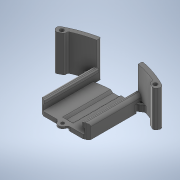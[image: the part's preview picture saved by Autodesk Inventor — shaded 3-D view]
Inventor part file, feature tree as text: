
AUTODESK INVENTOR PART (.ipt)
format: ipt  version: 2020 (Build 240168000, 168)  size: 1,011,712 bytes
history: native  units: mm
features: projected_geometry x25, other x11, sketch x11, extrude x10, fillet x3, chamfer x1
ambient origin geometry x8: Origin, YZ Plane, XZ Plane, XY Plane, X Axis, Y Axis, Z Axis, Center Point
bodies: Body1 (feature_tree)
feature tree (61):
  other  "Твердое тело1"
  sketch  "Эскиз1"
  other  "РабПлоскость4"
  sketch  "Эскиз2"
  other  "РабПлоскость5"
  sketch  "Эскиз3"
  other  "РабПлоскость6"
  sketch  "Эскиз4"
  other  "РабПлоскость7"
  sketch  "Эскиз5"
  other  "РабПлоскость8"
  sketch  "Эскиз6"
  extrude  "Выдавливание9"  TaperAngle=45.0deg  [1 undecoded]
  extrude  "Выдавливание10"  Depth=7.0mm
  other  "РабПлоскость1"
  extrude  "Выдавливание11"  Depth=20.0mm
  chamfer  "Фаска1"  Distance=7.0mm
  fillet  "Сопряжение1"  Radius=3.2mm
  fillet  "Сопряжение2"  Radius=59.0mm
  other  "РабПлоскость2"
  extrude  "Выдавливание12"  Depth=83.0mm
  other  "РабПлоскость9"
  sketch  "Эскиз9"
  extrude  "Выдавливание13"  Depth=69.0mm
  extrude  "Выдавливание14"  Depth=55.0mm
  other  "РабПлоскость3"
  extrude  "Выдавливание15"  Depth=3.0mm
  extrude  "Выдавливание16"  Depth=8.0mm
  extrude  "Выдавливание17"  Depth=5.0mm
  other  "РабПлоскость10"
  extrude  "Выдавливание18"  Depth=2.0mm
  fillet  "Сопряжение4"  Radius=40.0mm
  projected_geometry  "Спроецированная петля1"
  projected_geometry  "Спроецированная петля2"
  projected_geometry  "Спроецированная петля3"
  projected_geometry  "Спроецированная петля4"
  projected_geometry  "Спроецированная петля5"
  sketch  "Эскиз7"
  projected_geometry  "Спроецированная петля6"
  projected_geometry  "Спроецированная петля7"
  projected_geometry  "Спроецированная петля8"
  sketch  "Эскиз8"
  projected_geometry  "Спроецированная петля13"
  projected_geometry  "Спроецированная петля14"
  projected_geometry  "Спроецированная петля15"
  sketch  "Эскиз10"
  projected_geometry  "Спроецированная петля16"
  projected_geometry  "Спроецированная петля18"
  projected_geometry  "Спроецированная петля19"
  projected_geometry  "Спроецированная петля21"
  projected_geometry  "Спроецированная петля24"
  projected_geometry  "Спроецированная петля25"
  sketch  "Эскиз12"
  projected_geometry  "Спроецированная петля26"
  projected_geometry  "Спроецированная петля27"
  projected_geometry  "Спроецированная петля28"
  projected_geometry  "Спроецированная петля29"
  projected_geometry  "Спроецированная петля30"
  projected_geometry  "Спроецированная петля31"
  projected_geometry  "Спроецированная петля32"
  projected_geometry  "Спроецированная петля33"
note: 1 required parameter value undecoded (feature->parameter linkage not recoverable at this tier; creation-order binding heuristic only, values carry confidence <= 0.55)
